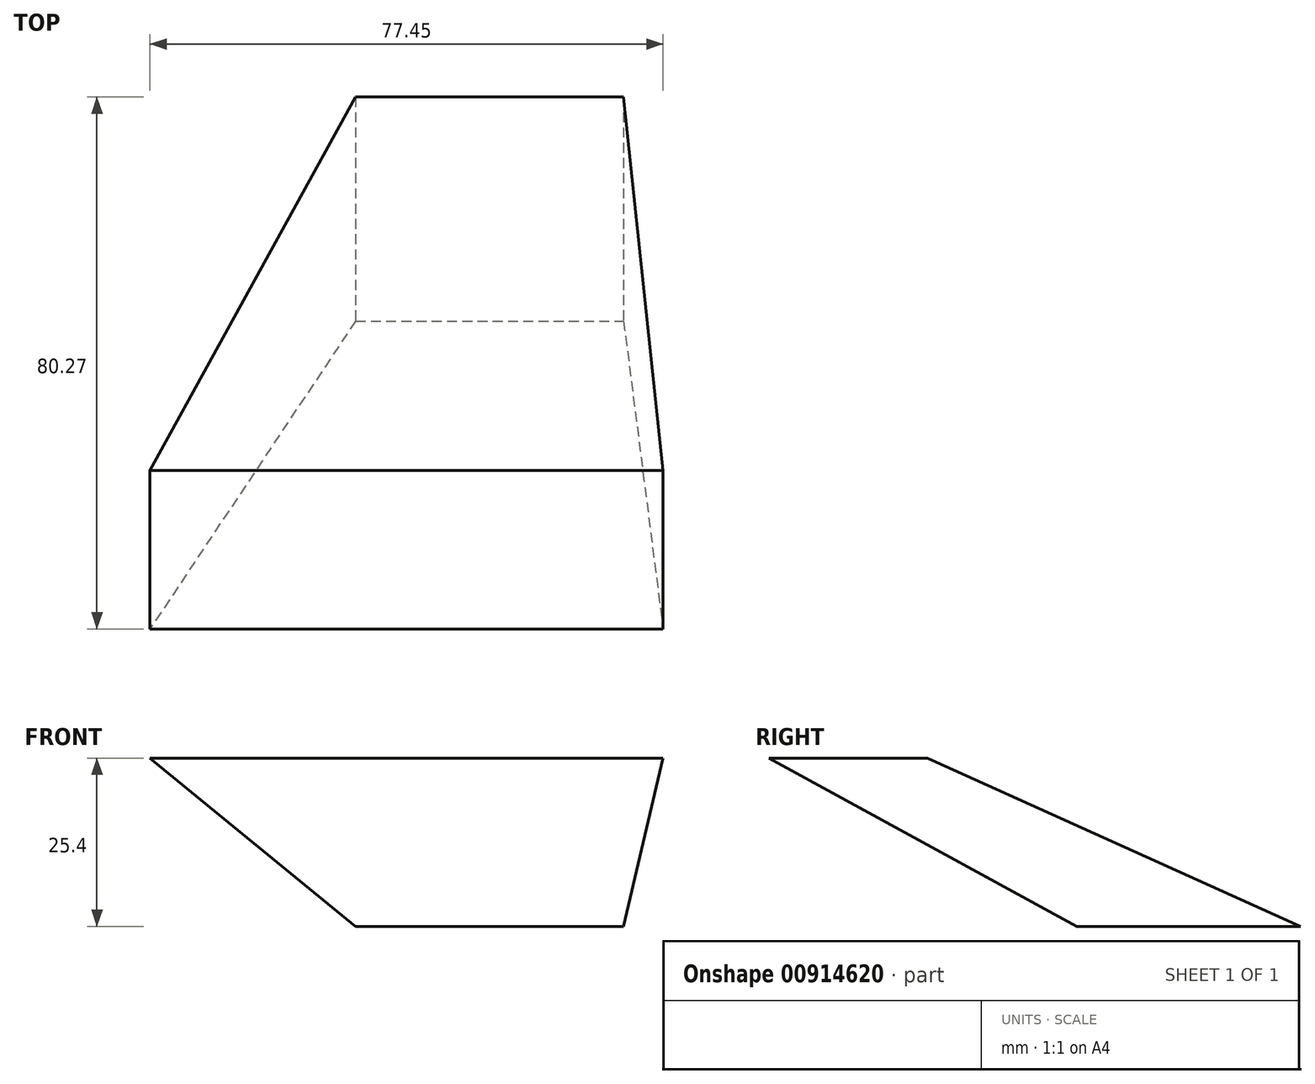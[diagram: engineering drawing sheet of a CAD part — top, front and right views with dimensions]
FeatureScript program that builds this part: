
annotation { "Feature Type Name" : "Feature", "Feature Type Description" : "" }
export const myFeature = defineFeature(function(context is Context, id is Id, definition is map)
    precondition{}
    {
        {
            var Q0;
            Q0=qCreatedBy(makeId("Top.planeOp"),FACE);
            var sketch = newSketch(context, id + "F0", { "sketchPlane" : qUnion([Q0])});
            skLineSegment(sketch, "E0.bottom", {"start": v(-50.31, 40.45) * mm, "end": v(-9.86, 40.45) * mm});
            skLineSegment(sketch, "E0.top", {"start": v(-50.31, 6.66) * mm, "end": v(-9.86, 6.66) * mm});
            skLineSegment(sketch, "E0.left", {"start": v(-50.31, 40.45) * mm, "end": v(-50.31, 6.66) * mm});
            skLineSegment(sketch, "E0.right", {"start": v(-9.86, 40.45) * mm, "end": v(-9.86, 6.66) * mm});
            skSolve(sketch);
        }
        {
            var Q0;
            Q0=qCreatedBy(makeId("Top.planeOp"),FACE);
            cPlane(context, id + "F1", {"entities" : qUnion([Q0]), "cplaneType" : CPlaneType.OFFSET, "offset" : 25.4 * mm, "width" : 152.4 * mm, "height" : 152.4 * mm});
        }
        {
            var Q0;
            Q0=qCreatedBy(id+"F1.planeOp",FACE);
            var sketch = newSketch(context, id + "F2", { "sketchPlane" : qUnion([Q0])});
            skLineSegment(sketch, "E1.bottom", {"start": v(-81.36, -15.89) * mm, "end": v(-3.9, -15.89) * mm});
            skLineSegment(sketch, "E1.top", {"start": v(-81.36, -39.82) * mm, "end": v(-3.9, -39.82) * mm});
            skLineSegment(sketch, "E1.left", {"start": v(-81.36, -15.89) * mm, "end": v(-81.36, -39.82) * mm});
            skLineSegment(sketch, "E1.right", {"start": v(-3.9, -15.89) * mm, "end": v(-3.9, -39.82) * mm});
            skSolve(sketch);
        }
        {
            var Q0;
            Q0=makeQuery(id+"F0.imprint","IMPRINT",FACE,{"disambiguationData":[TD([[makeQuery(id+"F0.imprint","IMPRINT",EDGE,{"derivedFrom":sQuery(id+"F0.wireOp",EDGE,"E0.bottom")}),-1.0]])]});
            var Q1;
            Q1=makeQuery(id+"F2.imprint","IMPRINT",FACE,{"disambiguationData":[TD([[makeQuery(id+"F2.imprint","IMPRINT",EDGE,{"derivedFrom":sQuery(id+"F2.wireOp",EDGE,"E1.bottom")}),-1.0]])]});
            loft(context, id + "F3", {"sheetProfilesArray" : [{ "sheetProfileEntities" : qUnion([Q0]) }, { "sheetProfileEntities" : qUnion([Q1]) }]});
        }
    });
